# Revit family: KEUCO_14909012037
name_source: partatom
category: Allgemeines Modell
revit_build: Autodesk Revit 2016 (Build: 20150220_1215(x64)
units: mm (PartAtom-declared; Revit-internal decimal feet)

## family parameters
Arbeitsebenenbasiert = Ja
Beim Laden mit Abzugskörper schneiden = Nein
Bemaßung runder Anschluss = Durchmesser verwenden
Gemeinsam genutzt = Nein
Immer vertikal = Nein
Kann Basisbauteil für Bewehrung sein = Nein
Raumberechnungspunkt = Nein
Teiletyp = Normal

## types (9) — shared parameters
Beschreibung = mit Seifenablage, linke Ausführung
Hersteller = KEUCO
Serie = Plan
URL = https://www.keuco.com
Verwendung = BI / DU / WA
Vorgabe-Ansicht = 1219 mm
zero-valued in all types: Gewicht

## per-type parameters (varying)
| type | Ausschreibungstext | Material Tablett | Rahmen Material |
| 14909012037 | KEUCO PLAN Winkelgriff 135° mit Seifenablage, linke Ausführung, 14909012037
hochglanzverchromter Winkelgriff 135° mit integrierter Seifenablage, 
in ästhetischem, funktionalem Design,
linke Ausführung,
speziell für Wannen-Bereich, als Hilfe zum Festhalten und Abstützen, 
mit integrierter Seifenablage aus Kunststoff (schlagzähes Polysterol), schwarzgrau (RAL 7021),
Ablagefläche 154 mm Breite, 23 mm Höhe, Tiefe 67 mm,
Winkelgriff bis 115 kg belastbar, antistatisch, leicht zu reinigen,
Außenmaß gesamt 444/201 mm,
Rohrdurchmesser 25 mm, 3 Befestigungspunkte, 
Gesamtbreite 444 mm, Gesamthöhe 201 mm, 
Ausladung 108 mm, Wandabstand 83 mm
Der Winkelgriff wird verdeckt angebracht

Lieferung inkl. korrosionsfreiem Befestigungsmaterial | schwarzgrau (RAL 7021) | verchromt |
| 14909012038 | KEUCO PLAN Winkelgriff 135° mit Seifenablage, linke Ausführung, 14909012038
hochglanzverchromter Winkelgriff 135° mit integrierter Seifenablage, 
in ästhetischem, funktionalem Design
linke Ausführung,
speziell für Wannen-Bereich, als Hilfe zum Festhalten und Abstützen, 
mit integrierter Seifenablage aus Kunststoff (schlagzähes Polysterol), lichtgrau (RAL 7035),
Ablagefläche 154 mm Breite, 23 mm Höhe, Tiefe 67 mm,
Winkelgriff bis 115 kg belastbar, antistatisch, leicht zu reinigen,
Außenmaß gesamt 444/201 mm,
Rohrdurchmesser 25 mm, 3 Befestigungspunkte, 
Gesamtbreite 444 mm, Gesamthöhe 201 mm, 
Ausladung 108 mm, Wandabstand 83 mm
Der Winkelgriff wird verdeckt angebracht

Lieferung inkl. korrosionsfreiem Befestigungsmaterial | Lichtgrau (RAL 7035) | verchromt |
| 14909012051 | KEUCO PLAN Winkelgriff 135° mit Seifenablage, linke Ausführung, 14909012051
hochglanzverchromter Winkelgriff 135° mit integrierter Seifenablage, 
in ästhetischem, funktionalem Design
linke Ausführung,
speziell für Wannen-Bereich, als Hilfe zum Festhalten und Abstützen, 
mit integrierter Seifenablage aus Kunststoff (schlagzähes Polysterol), weiß (RAL 9010),
Ablagefläche 154 mm Breite, 23 mm Höhe, Tiefe 67 mm,
Winkelgriff bis 115 kg belastbar, antistatisch, leicht zu reinigen,
Außenmaß gesamt 444/201 mm,
Rohrdurchmesser 25 mm, 3 Befestigungspunkte, 
Gesamtbreite 444 mm, Gesamthöhe 201 mm, 
Ausladung 108 mm, Wandabstand 83 mm
Der Winkelgriff wird verdeckt angebracht

Lieferung inkl. korrosionsfreiem Befestigungsmaterial | Weiß (RAL 9010) | verchromt |
| 14909072037 | KEUCO PLAN Winkelgriff 135° mit Seifenablage, linke Ausführung, 14909072037
Winkelgriff 135° aus hochwertigem Edelstahl mit integrierter Seifenablage, 
in ästhetischem, funktionalem Design
linke Ausführung,
speziell für Wannen-Bereich, als Hilfe zum Festhalten und Abstützen, 
mit integrierter Seifenablage aus Kunststoff (schlagzähes Polysterol), schwarzgrau (RAL 7021),
Ablagefläche 154 mm Breite, 23 mm Höhe, Tiefe 67 mm,
Winkelgriff bis 115 kg belastbar, antistatisch, leicht zu reinigen,
Außenmaß gesamt 444/201 mm,
Rohrdurchmesser 25 mm, 3 Befestigungspunkte, 
Gesamtbreite 444 mm, Gesamthöhe 201 mm, 
Ausladung 108 mm, Wandabstand 83 mm
Der Winkelgriff wird verdeckt angebracht

Lieferung inkl. korrosionsfreiem Befestigungsmaterial | schwarzgrau (RAL 7021) | Edelstahl |
| 14909072038 | KEUCO PLAN Winkelgriff 135° mit Seifenablage, linke Ausführung, 14909072038
Winkelgriff 135° aus hochwertigem Edelstahl mit integrierter Seifenablage, 
in ästhetischem, funktionalem Design
linke Ausführung,
speziell für Wannen-Bereich, als Hilfe zum Festhalten und Abstützen, 
mit integrierter Seifenablage aus Kunststoff (schlagzähes Polysterol), .lichtgrau (RAL 7035,
Ablagefläche 154 mm Breite, 23 mm Höhe, Tiefe 67 mm,
Winkelgriff bis 115 kg belastbar, antistatisch, leicht zu reinigen,
Außenmaß gesamt 444/201 mm,
Rohrdurchmesser 25 mm, 3 Befestigungspunkte, 
Gesamtbreite 444 mm, Gesamthöhe 201 mm, 
Ausladung 108 mm, Wandabstand 83 mm
Der Winkelgriff wird verdeckt angebracht

Lieferung inkl. korrosionsfreiem Befestigungsmaterial | schwarzgrau (RAL 7021) | verchromt |
| 14909072051 | KEUCO PLAN Winkelgriff 135° mit Seifenablage, linke Ausführung, 14909072051
Winkelgriff 135° aus hochwertigem Edelstahl mit integrierter Seifenablage, 
in ästhetischem, funktionalem Design
linke Ausführung,
speziell für Wannen-Bereich, als Hilfe zum Festhalten und Abstützen, 
mit integrierter Seifenablage aus Kunststoff (schlagzähes Polysterol), weiß (RAL 9010
Ablagefläche 154 mm Breite, 23 mm Höhe, Tiefe 67 mm,
Winkelgriff bis 115 kg belastbar, antistatisch, leicht zu reinigen,
Außenmaß gesamt 444/201 mm,
Rohrdurchmesser 25 mm, 3 Befestigungspunkte, 
Gesamtbreite 444 mm, Gesamthöhe 201 mm, 
Ausladung 108 mm, Wandabstand 83 mm
Der Winkelgriff wird verdeckt angebracht

Lieferung inkl. korrosionsfreiem Befestigungsmaterial | Weiß (RAL 9010) | Edelstahl |
| 14909172037 | KEUCO PLAN Winkelgriff 135° mit Seifenablage, linke Ausführung, 14909172037
Winkelgriff 135° aus silber-eloxiertem Aluminium mit integrierter Seifenablage, 
in ästhetischem, funktionalem Design
linke Ausführung,
speziell für Wannen-Bereich, als Hilfe zum Festhalten und Abstützen, 
mit integrierter Seifenablage aus Kunststoff (schlagzähes Polysterol), schwarzgrau (RAL 7021),
Ablagefläche 154 mm Breite, 23 mm Höhe, Tiefe 67 mm,
Winkelgriff bis 115 kg belastbar, antistatisch, leicht zu reinigen,
Außenmaß gesamt 444/201 mm,
Rohrdurchmesser 25 mm, 3 Befestigungspunkte, 
Gesamtbreite 444 mm, Gesamthöhe 201 mm, 
Ausladung 108 mm, Wandabstand 83 mm
Der Winkelgriff wird verdeckt angebracht

Lieferung inkl. korrosionsfreiem Befestigungsmaterial | Aluminium 1100-H18 | Aluminium 1100-H18 |
| 14909172038 | KEUCO PLAN Winkelgriff 135° mit Seifenablage, linke Ausführung, 14909172038
Winkelgriff 135° aus silber-eloxiertem Aluminium mit integrierter Seifenablage, 
in ästhetischem, funktionalem Design
linke Ausführung,
speziell für Wannen-Bereich, als Hilfe zum Festhalten und Abstützen, 
mit integrierter Seifenablage aus Kunststoff (schlagzähes Polysterol), lichtgrau (RAL 7035),
Ablagefläche 154 mm Breite, 23 mm Höhe, Tiefe 67 mm,
Winkelgriff bis 115 kg belastbar, antistatisch, leicht zu reinigen,
Außenmaß gesamt 444/201 mm,
Rohrdurchmesser 25 mm, 3 Befestigungspunkte, 
Gesamtbreite 444 mm, Gesamthöhe 201 mm, 
Ausladung 108 mm, Wandabstand 83 mm
Der Winkelgriff wird verdeckt angebracht

Lieferung inkl. korrosionsfreiem Befestigungsmaterial | Lichtgrau (RAL 7035) | Aluminium 1100-H18 |
| 14909172051 | KEUCO PLAN Winkelgriff 135° mit Seifenablage, linke Ausführung, 14909172051
Winkelgriff 135° aus silber-eloxiertem Aluminium mit integrierter Seifenablage, 
in ästhetischem, funktionalem Design
linke Ausführung,
speziell für Wannen-Bereich, als Hilfe zum Festhalten und Abstützen, 
mit integrierter Seifenablage aus Kunststoff (schlagzähes Polysterol), weiß (RAL 9010),
Ablagefläche 154 mm Breite, 23 mm Höhe, Tiefe 67 mm,
Winkelgriff bis 115 kg belastbar, antistatisch, leicht zu reinigen,
Außenmaß gesamt 444/201 mm,
Rohrdurchmesser 25 mm, 3 Befestigungspunkte, 
Gesamtbreite 444 mm, Gesamthöhe 201 mm, 
Ausladung 108 mm, Wandabstand 83 mm
Der Winkelgriff wird verdeckt angebracht

Lieferung inkl. korrosionsfreiem Befestigungsmaterial | Weiß (RAL 9010) | Aluminium 1100-H18 |

note: column(s) folded — value = type name in every type: Artikelnummer

## geometry (parser evidence)
native form markers: Blend x4, Sweep x3
no freeform markers — native parametric forms only
